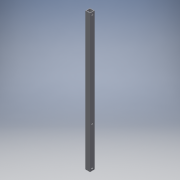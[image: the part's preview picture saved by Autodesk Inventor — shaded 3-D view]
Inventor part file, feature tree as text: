
AUTODESK INVENTOR PART (.ipt)
format: ipt  version: 2016 (Build 200138000, 138)  size: 145,920 bytes
history: native  units: in
note: dims shown in document units (in); Inventor stores cm internally (conversion verified against a paired STEP export)
features: extrude x5, sketch x5
ambient origin geometry x8: Origin, YZ Plane, XZ Plane, XY Plane, X Axis, Y Axis, Z Axis, Center Point
bodies: Solid1 (feature_tree)
feature tree (10):
  extrude  "Extrusion1"  Depth=1.0in
  extrude  "Extrusion3"  Depth=0.125in
  sketch  "Sketch4"  dims[d4=0.125in d6=0.125in]
  extrude  "Extrusion5"  Depth=0.125in
  extrude  "Extrusion7"  Depth=30.0in
  extrude  "Extrusion8"  Depth=1.0in
  sketch  "Sketch1"  dims[d0=1.0in d1=1.0in]
  sketch  "Sketch3"  dims[d2=0.125in d3=0.125in]
  sketch  "Sketch5"  dims[d7=30.0in d8=0.0in d17=0.4in]
  sketch  "Sketch6"  dims[d18=0.5in d19=0.5in d20=1.0in d21=0.0in d22=0.5in d23=0.5in d29=0.375in d30=0.5in d31=0.5in d32=1.0in d33=0.0in d37=1.0in d38=0.0in d40=0.875in d41=0.5in d42=8.9in d43=1.0in d44=0.0in]
